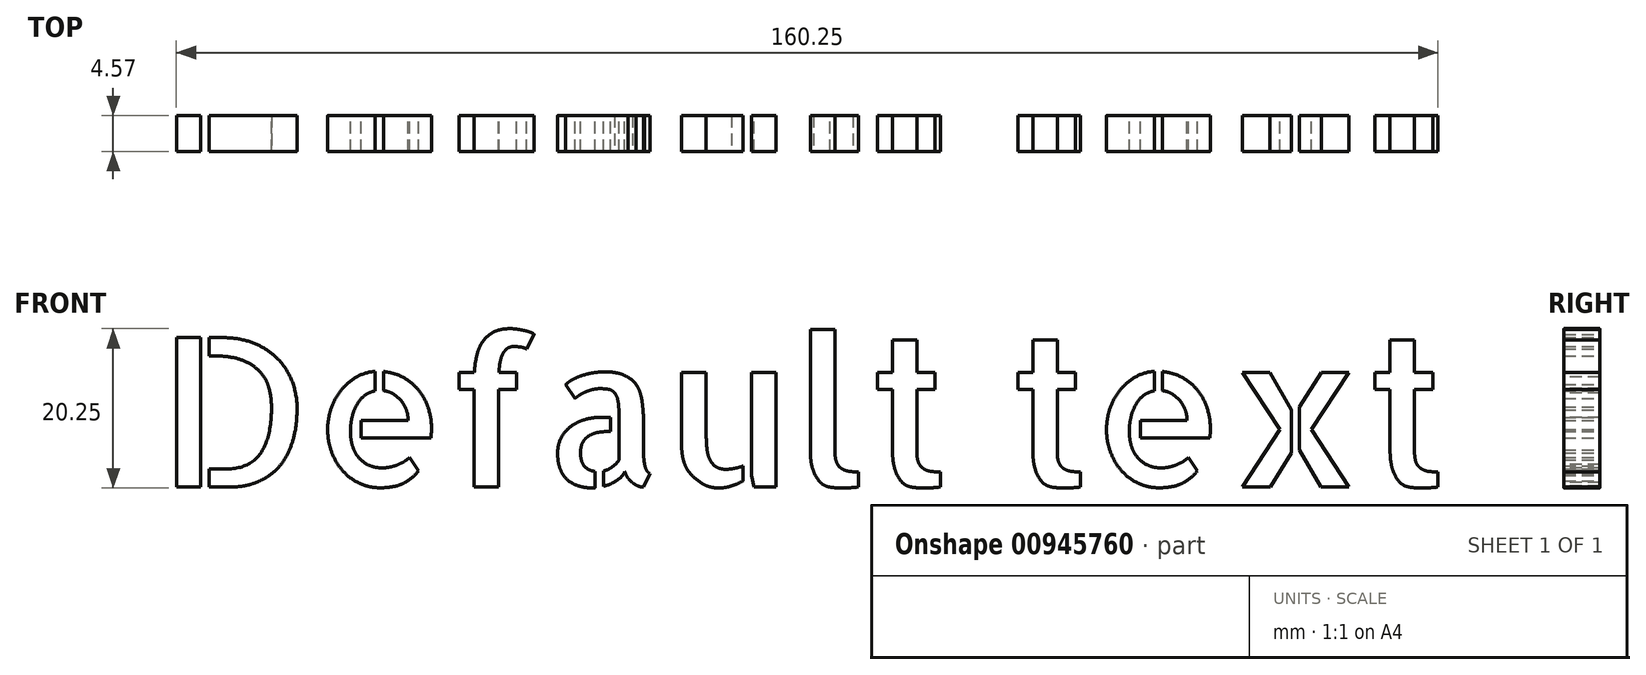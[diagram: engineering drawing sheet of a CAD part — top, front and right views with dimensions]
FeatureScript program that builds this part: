
annotation { "Feature Type Name" : "Feature", "Feature Type Description" : "" }
export const myFeature = defineFeature(function(context is Context, id is Id, definition is map)
    precondition{}
    {
        {
            var Q0;
            Q0=qCreatedBy(makeId("Front.planeOp"),FACE);
            var sketch = newSketch(context, id + "F0", { "sketchPlane" : qUnion([Q0])});
            skText(sketch, "E0", { "text": "Default text", "fontName": "AllertaStencil-Regular.ttf"});
            const initialGuessF0  = {"E0": [-0.06424, 0.03533, 1, 0, 0.01899]};
            skSetInitialGuess(sketch, initialGuessF0);
            skSolve(sketch);
        }
        {
            var Q0;
            Q0 = qSketchRegion(id + "F0", true);
            extrude(context, id + "F1", {"entities" : qUnion([Q0]), "depth" : 4.57 * mm, "offsetDistance" : 25.4 * mm});
        }
    });
